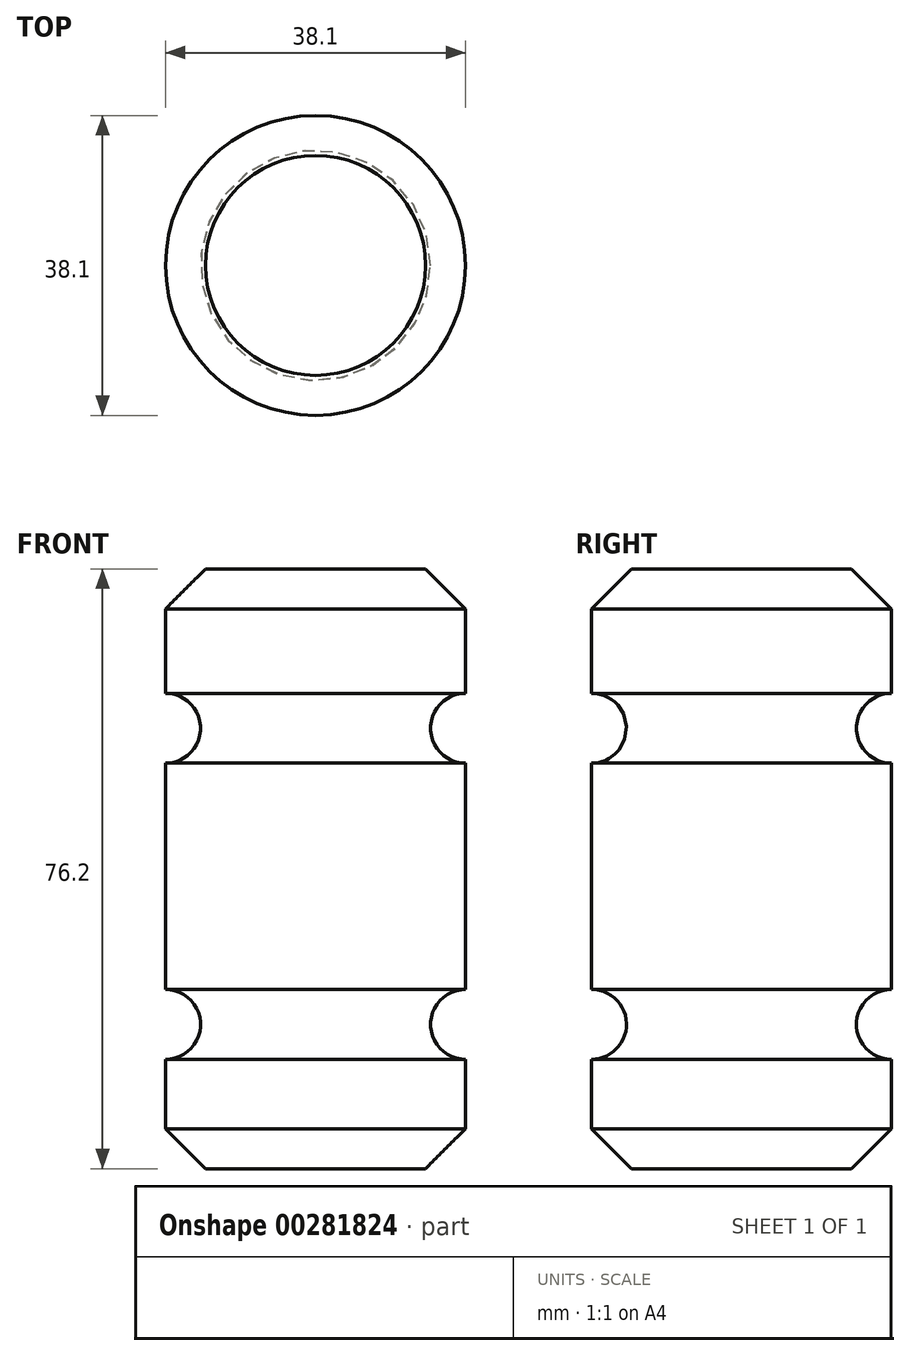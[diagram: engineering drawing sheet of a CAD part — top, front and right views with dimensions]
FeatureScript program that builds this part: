
annotation { "Feature Type Name" : "Feature", "Feature Type Description" : "" }
export const myFeature = defineFeature(function(context is Context, id is Id, definition is map)
    precondition{}
    {
        {
            var Q0;
            Q0=qCreatedBy(makeId("Front.planeOp"),FACE);
            var sketch = newSketch(context, id + "F0", { "sketchPlane" : qUnion([Q0])});
            skLineSegment(sketch, "E0", {"start": v(0, 0) * mm, "end": v(0, 13.89) * mm});
            skLineSegment(sketch, "E1", {"start": v(0, 76.2) * mm, "end": v(-19.05, 76.2) * mm});
            skLineSegment(sketch, "E2", {"start": v(-19.05, 76.2) * mm, "end": v(-19.05, 0) * mm});
            skLineSegment(sketch, "E3", {"start": v(-19.05, 0) * mm, "end": v(0, 0) * mm});
            skArc(sketch, "E4", {"start": v(0, 60.4) * mm, "mid": v(-4.44, 55.95) * mm, "end": v(0, 51.5) * mm});
            skArc(sketch, "E5", {"start": v(0, 22.78) * mm, "mid": v(-4.45, 18.33) * mm, "end": v(0, 13.89) * mm});
            skLineSegment(sketch, "E6.trimOffspring", {"start": v(0, 60.4) * mm, "end": v(0, 76.2) * mm});
            skLineSegment(sketch, "E7.trimOffspring", {"start": v(0, 22.78) * mm, "end": v(0, 51.5) * mm});
            skSolve(sketch);
        }
        {
            var Q0;
            Q0=makeQuery(id+"F0.imprint","IMPRINT",FACE,{"disambiguationData":[TD([[makeQuery(id+"F0.imprint","IMPRINT",EDGE,{"derivedFrom":sQuery(id+"F0.wireOp",EDGE,"E0")}),1.0]])]});
            var Q1;
            Q1=sQuery(id+"F0.wireOp",EDGE,"E2");
            revolve(context, id + "F1", {"entities" : qUnion([Q0]), "axis" : qUnion([Q1]), "revolveType" : RevolveType.FULL});
        }
        {
            var Q0;
            Q0=makeQuery(id+"F1.opRevolve","SWEPT_EDGE",EDGE,{"disambiguationData":[OSD([sQuery(id+"F0.wireOp",EDGE,"E1"),sQuery(id+"F0.wireOp",EDGE,"E6.trimOffspring")])]});
            var Q1;
            Q1=makeQuery(id+"F1.opRevolve","SWEPT_EDGE",EDGE,{"disambiguationData":[OSD([sQuery(id+"F0.wireOp",EDGE,"E0"),sQuery(id+"F0.wireOp",EDGE,"E3")])]});
            chamfer(context, id + "F2", {"entities" : qUnion([Q0, Q1]), "width" : 5.08 * mm, "tangentPropagation" : true});
        }
    });
